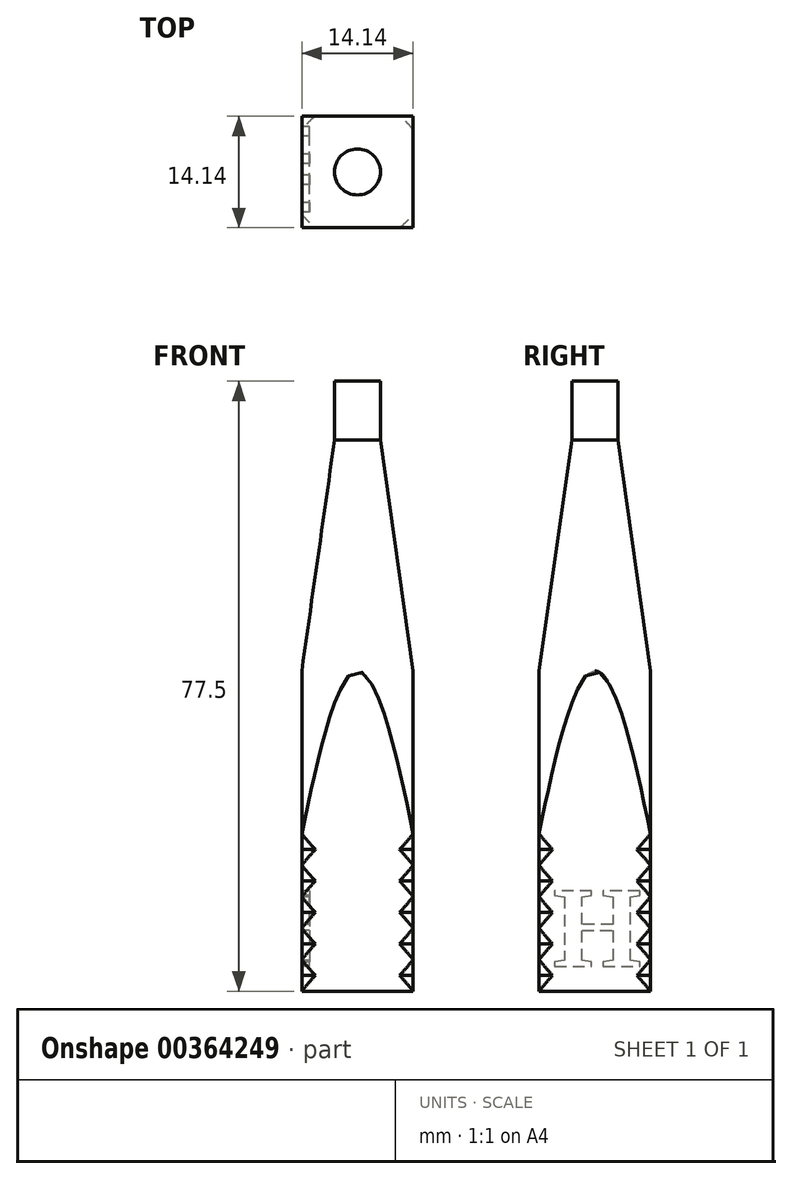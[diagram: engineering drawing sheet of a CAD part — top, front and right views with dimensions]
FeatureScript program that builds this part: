
annotation { "Feature Type Name" : "Feature", "Feature Type Description" : "" }
export const myFeature = defineFeature(function(context is Context, id is Id, definition is map)
    precondition{}
    {
        {
            var Q0;
            Q0=qCreatedBy(makeId("Top.planeOp"),FACE);
            var sketch = newSketch(context, id + "F0", { "sketchPlane" : qUnion([Q0])});
            skCircle(sketch, "E0", {"center": v(0, 0) * mm, "radius": 10 * mm, "construction": true});
            skLineSegment(sketch, "E1", {"start": v(-7.07, -7.07) * mm, "end": v(7.07, -7.07) * mm});
            skLineSegment(sketch, "E2", {"start": v(7.07, -7.07) * mm, "end": v(7.07, 7.07) * mm});
            skLineSegment(sketch, "E3", {"start": v(7.07, 7.07) * mm, "end": v(-7.07, 7.07) * mm});
            skLineSegment(sketch, "E4", {"start": v(-7.07, 7.07) * mm, "end": v(-7.07, -7.07) * mm});
            skSolve(sketch);
        }
        {
            var Q0;
            Q0=makeQuery(id+"F0.imprint","IMPRINT",FACE,{"disambiguationData":[TD([[makeQuery(id+"F0.imprint","IMPRINT",EDGE,{"derivedFrom":sQuery(id+"F0.wireOp",EDGE,"wcAVtdV2-EokJ-VWxA-gxln-DFa8Tj28oSSP")}),-1.0]])]});
            var Q1;
            Q1=makeQuery(id+"F0.imprint","IMPRINT",FACE,{"disambiguationData":[TD([[makeQuery(id+"F0.imprint","IMPRINT",EDGE,{"derivedFrom":sQuery(id+"F0.wireOp",EDGE,"E1")}),1.0]])]});
            extrude(context, id + "F1", {"entities" : qUnion([Q0, Q1]), "offsetDistance" : 25 * mm, "depth" : 20 * mm});
        }
        {
            var Q0;
            Q0=qCreatedBy(makeId("Right.planeOp"),FACE);
            var sketch = newSketch(context, id + "F2", { "sketchPlane" : qUnion([Q0]), "disableImprinting" : false});
            skLineSegment(sketch, "E5", {"start": v(-2.92, 70) * mm, "end": v(-10, 20) * mm});
            skLineSegment(sketch, "E6", {"start": v(-10, 20) * mm, "end": v(0, 20) * mm});
            skLineSegment(sketch, "E7", {"start": v(0, 20) * mm, "end": v(0, 70) * mm});
            skLineSegment(sketch, "E8", {"start": v(-2.92, 70) * mm, "end": v(0, 70) * mm, "construction": true});
            skLineSegment(sketch, "E9", {"start": v(-2.92, 70) * mm, "end": v(-2.92, 76.5) * mm});
            skLineSegment(sketch, "E10", {"start": v(-2.92, 76.5) * mm, "end": v(0, 76.5) * mm});
            skLineSegment(sketch, "E11", {"start": v(0, 76.5) * mm, "end": v(0, 70) * mm});
            skSolve(sketch);
        }
        {
            var Q0;
            Q0=makeQuery(id+"F2.imprint","IMPRINT",FACE,{"disambiguationData":[TD([[makeQuery(id+"F2.imprint","IMPRINT",EDGE,{"derivedFrom":sQuery(id+"F2.wireOp",EDGE,"E5")}),1.0]])]});
            var Q1;
            Q1=sQuery(id+"F2.wireOp",EDGE,"E7");
            revolve(context, id + "F3", {"operationType" : NewBodyOperationType.ADD, "surfaceOperationType" : NewSurfaceOperationType.NEW, "entities" : qUnion([Q0]), "axis" : qUnion([Q1]), "revolveType" : RevolveType.FULL});
        }
        {
            var Q0;
            {var subQ0=makeQuery(id+"F3.opRevolve","SWEPT_FACE",FACE,{"disambiguationData":[OSD([sQuery(id+"F2.wireOp",EDGE,"E6")])]});Q0=makeQuery(id+"F3.boolean.opBoolean","SPLIT",FACE,{"disambiguationData":[TD([makeQuery(id+"F1.opExtrude","SWEPT_FACE",FACE,{"disambiguationData":[OSD([sQuery(id+"F0.wireOp",EDGE,"DRX1ucCg-DjaC-MiWL-Vcy4-4rUpKsN5Zpb4")])]}),makeQuery(id+"F1.opExtrude","SWEPT_FACE",FACE,{"disambiguationData":[OSD([sQuery(id+"F0.wireOp",EDGE,"OoSLFpEq-8l7p-tjY5-sLpR-2C7ZDxoHFw3J")])]}),makeQuery(id+"F1.opExtrude","SWEPT_FACE",FACE,{"disambiguationData":[OSD([sQuery(id+"F0.wireOp",EDGE,"05nhAoml-3LFM-mqCG-1RSL-4N1tzizKSWDP")])]}),makeQuery(id+"F3.opRevolve","SWEPT_FACE",FACE,{"disambiguationData":[OSD([sQuery(id+"F2.wireOp",EDGE,"E5")])]}),subQ0])],"derivedFrom":subQ0});}
            var Q1;
            {var subQ0=makeQuery(id+"F3.opRevolve","SWEPT_FACE",FACE,{"disambiguationData":[OSD([sQuery(id+"F2.wireOp",EDGE,"E6")])]});Q1=makeQuery(id+"F3.boolean.opBoolean","SPLIT",FACE,{"disambiguationData":[TD([makeQuery(id+"F1.opExtrude","SWEPT_FACE",FACE,{"disambiguationData":[OSD([sQuery(id+"F0.wireOp",EDGE,"wcAVtdV2-EokJ-VWxA-gxln-DFa8Tj28oSSP")])]}),makeQuery(id+"F1.opExtrude","SWEPT_FACE",FACE,{"disambiguationData":[OSD([sQuery(id+"F0.wireOp",EDGE,"OoSLFpEq-8l7p-tjY5-sLpR-2C7ZDxoHFw3J")])]}),makeQuery(id+"F1.opExtrude","SWEPT_FACE",FACE,{"disambiguationData":[OSD([sQuery(id+"F0.wireOp",EDGE,"05nhAoml-3LFM-mqCG-1RSL-4N1tzizKSWDP")])]}),makeQuery(id+"F3.opRevolve","SWEPT_FACE",FACE,{"disambiguationData":[OSD([sQuery(id+"F2.wireOp",EDGE,"E5")])]}),subQ0])],"derivedFrom":subQ0});}
            var Q2;
            {var subQ0=makeQuery(id+"F3.opRevolve","SWEPT_FACE",FACE,{"disambiguationData":[OSD([sQuery(id+"F2.wireOp",EDGE,"E6")])]});Q2=makeQuery(id+"F3.boolean.opBoolean","SPLIT",FACE,{"disambiguationData":[TD([makeQuery(id+"F1.opExtrude","SWEPT_FACE",FACE,{"disambiguationData":[OSD([sQuery(id+"F0.wireOp",EDGE,"tCxQUq4m-YUaR-PUol-IUOQ-F8SX8qTUi1zU")])]}),makeQuery(id+"F1.opExtrude","SWEPT_FACE",FACE,{"disambiguationData":[OSD([sQuery(id+"F0.wireOp",EDGE,"DRX1ucCg-DjaC-MiWL-Vcy4-4rUpKsN5Zpb4")])]}),makeQuery(id+"F1.opExtrude","SWEPT_FACE",FACE,{"disambiguationData":[OSD([sQuery(id+"F0.wireOp",EDGE,"OoSLFpEq-8l7p-tjY5-sLpR-2C7ZDxoHFw3J")])]}),makeQuery(id+"F3.opRevolve","SWEPT_FACE",FACE,{"disambiguationData":[OSD([sQuery(id+"F2.wireOp",EDGE,"E5")])]}),subQ0])],"derivedFrom":subQ0});}
            var Q3;
            {var subQ0=makeQuery(id+"F3.opRevolve","SWEPT_FACE",FACE,{"disambiguationData":[OSD([sQuery(id+"F2.wireOp",EDGE,"E6")])]});Q3=makeQuery(id+"F3.boolean.opBoolean","SPLIT",FACE,{"disambiguationData":[TD([makeQuery(id+"F1.opExtrude","SWEPT_FACE",FACE,{"disambiguationData":[OSD([sQuery(id+"F0.wireOp",EDGE,"Q6e6Ubm2-IwZc-4Gsr-nhjH-oOF9pMSWuxT1")])]}),makeQuery(id+"F1.opExtrude","SWEPT_FACE",FACE,{"disambiguationData":[OSD([sQuery(id+"F0.wireOp",EDGE,"tCxQUq4m-YUaR-PUol-IUOQ-F8SX8qTUi1zU")])]}),makeQuery(id+"F1.opExtrude","SWEPT_FACE",FACE,{"disambiguationData":[OSD([sQuery(id+"F0.wireOp",EDGE,"DRX1ucCg-DjaC-MiWL-Vcy4-4rUpKsN5Zpb4")])]}),makeQuery(id+"F3.opRevolve","SWEPT_FACE",FACE,{"disambiguationData":[OSD([sQuery(id+"F2.wireOp",EDGE,"E5")])]}),subQ0])],"derivedFrom":subQ0});}
            var Q4;
            {var subQ0=makeQuery(id+"F3.opRevolve","SWEPT_FACE",FACE,{"disambiguationData":[OSD([sQuery(id+"F2.wireOp",EDGE,"E6")])]});Q4=makeQuery(id+"F3.boolean.opBoolean","SPLIT",FACE,{"disambiguationData":[TD([makeQuery(id+"F1.opExtrude","SWEPT_FACE",FACE,{"disambiguationData":[OSD([sQuery(id+"F0.wireOp",EDGE,"wcAVtdV2-EokJ-VWxA-gxln-DFa8Tj28oSSP")])]}),makeQuery(id+"F1.opExtrude","SWEPT_FACE",FACE,{"disambiguationData":[OSD([sQuery(id+"F0.wireOp",EDGE,"Q6e6Ubm2-IwZc-4Gsr-nhjH-oOF9pMSWuxT1")])]}),makeQuery(id+"F1.opExtrude","SWEPT_FACE",FACE,{"disambiguationData":[OSD([sQuery(id+"F0.wireOp",EDGE,"tCxQUq4m-YUaR-PUol-IUOQ-F8SX8qTUi1zU")])]}),makeQuery(id+"F3.opRevolve","SWEPT_FACE",FACE,{"disambiguationData":[OSD([sQuery(id+"F2.wireOp",EDGE,"E5")])]}),subQ0])],"derivedFrom":subQ0});}
            var Q5;
            {var subQ0=makeQuery(id+"F3.opRevolve","SWEPT_FACE",FACE,{"disambiguationData":[OSD([sQuery(id+"F2.wireOp",EDGE,"E6")])]});Q5=makeQuery(id+"F3.boolean.opBoolean","SPLIT",FACE,{"disambiguationData":[TD([makeQuery(id+"F1.opExtrude","SWEPT_FACE",FACE,{"disambiguationData":[OSD([sQuery(id+"F0.wireOp",EDGE,"wcAVtdV2-EokJ-VWxA-gxln-DFa8Tj28oSSP")])]}),makeQuery(id+"F1.opExtrude","SWEPT_FACE",FACE,{"disambiguationData":[OSD([sQuery(id+"F0.wireOp",EDGE,"Q6e6Ubm2-IwZc-4Gsr-nhjH-oOF9pMSWuxT1")])]}),makeQuery(id+"F1.opExtrude","SWEPT_FACE",FACE,{"disambiguationData":[OSD([sQuery(id+"F0.wireOp",EDGE,"05nhAoml-3LFM-mqCG-1RSL-4N1tzizKSWDP")])]}),makeQuery(id+"F3.opRevolve","SWEPT_FACE",FACE,{"disambiguationData":[OSD([sQuery(id+"F2.wireOp",EDGE,"E5")])]}),subQ0])],"derivedFrom":subQ0});}
            extrude(context, id + "F4", {"entities" : qUnion([Q0, Q1, Q2, Q3, Q4, Q5]), "operationType" : NewBodyOperationType.REMOVE, "oppositeDirection" : true, "offsetDistance" : 25 * mm, "depth" : 25 * mm});
        }
        {
            var Q0;
            Q0=qCreatedBy(makeId("Front.planeOp"),FACE);
            var sketch = newSketch(context, id + "F5", { "sketchPlane" : qUnion([Q0])});
            skLineSegment(sketch, "E12", {"start": v(-10, 20) * mm, "end": v(-10, 0) * mm});
            skLineSegment(sketch, "E13", {"start": v(-10, 20) * mm, "end": v(-8.86, 18) * mm});
            skLineSegment(sketch, "E14", {"start": v(-8.86, 18) * mm, "end": v(-10, 16) * mm});
            skLineSegment(sketch, "E15", {"start": v(-10, 20) * mm, "end": v(-10, 16) * mm, "construction": true});
            skLineSegment(sketch, "E16.0.1.0", {"start": v(-10, 16) * mm, "end": v(-8.86, 14) * mm});
            skLineSegment(sketch, "E16.0.1.1", {"start": v(-8.86, 14) * mm, "end": v(-10, 12) * mm});
            skLineSegment(sketch, "E16.0.2.0", {"start": v(-10, 12) * mm, "end": v(-8.86, 10) * mm});
            skLineSegment(sketch, "E16.0.2.1", {"start": v(-8.86, 10) * mm, "end": v(-10, 8) * mm});
            skLineSegment(sketch, "E16.0.3.0", {"start": v(-10, 8) * mm, "end": v(-8.86, 6) * mm});
            skLineSegment(sketch, "E16.0.3.1", {"start": v(-8.86, 6) * mm, "end": v(-10, 4) * mm});
            skLineSegment(sketch, "E16.0.4.0", {"start": v(-10, 4) * mm, "end": v(-8.86, 2) * mm});
            skLineSegment(sketch, "E16.0.4.1", {"start": v(-8.86, 2) * mm, "end": v(-10, 0) * mm});
            skLineSegment(sketch, "E16.direction1", {"start": v(-10, 20) * mm, "end": v(15, 20) * mm, "construction": true});
            skLineSegment(sketch, "E17", {"start": v(0, 11.1) * mm, "end": v(0, 0) * mm, "construction": true});
            skLineSegment(sketch, "E18", {"start": v(-8.86, 18) * mm, "end": v(-10, 18) * mm, "construction": true});
            skLineSegment(sketch, "E19", {"start": v(-8.86, 14) * mm, "end": v(-10, 14) * mm, "construction": true});
            skLineSegment(sketch, "E20", {"start": v(-8.86, 10) * mm, "end": v(-10, 10) * mm, "construction": true});
            skLineSegment(sketch, "E21", {"start": v(-8.86, 6) * mm, "end": v(-10, 6) * mm, "construction": true});
            skLineSegment(sketch, "E22", {"start": v(-8.86, 2) * mm, "end": v(-10, 2) * mm, "construction": true});
            skSolve(sketch);
        }
        {
            var Q0;
            Q0=qSketchRegion(id+"F5",true);
            var Q1;
            Q1=sQuery(id+"F5.wireOp",EDGE,"E17");
            revolve(context, id + "F6", {"operationType" : NewBodyOperationType.REMOVE, "entities" : qUnion([Q0]), "axis" : qUnion([Q1]), "revolveType" : RevolveType.FULL});
        }
        {
            var Q0;
            Q0=makeQuery(id+"F3.opRevolve","SWEPT_FACE",FACE,{"disambiguationData":[OSD([sQuery(id+"F2.wireOp",EDGE,"E10")])]});
            extrude(context, id + "F7", {"entities" : qUnion([Q0]), "operationType" : NewBodyOperationType.ADD, "offsetDistance" : 25 * mm, "depth" : 1 * mm});
        }
        {
            var Q0;
            {var subQ0=sQuery(id+"F0.wireOp",EDGE,"E4");Q0=makeQuery(id+"F4.boolean.opBoolean","MERGE",FACE,{"derivedFrom":[makeQuery(id+"F1.opExtrude","SWEPT_FACE",FACE,{"disambiguationData":[OSD([subQ0])]})],"fromTools":[makeQuery(id+"F4.opExtrude","SWEPT_FACE",FACE,{"disambiguationData":[OSD([subQ0])]})]});}
            var sketch = newSketch(context, id + "F8", { "sketchPlane" : qUnion([Q0])});
            skText(sketch, "E23", { "text": "H", "fontName": "Tinos-Bold.ttf"});
            const initialGuessF8  = {"E23": [-0.006, 0.00318, 1, 0, 0.01049]};
            skSetInitialGuess(sketch, initialGuessF8);
            skSolve(sketch);
        }
        {
            var Q0;
            Q0=makeQuery(id+"F8.imprint","IMPRINT",FACE,{"disambiguationData":[TD([[makeQuery(id+"F8.imprint","IMPRINT",EDGE,{"derivedFrom":sQuery(id+"F8.wireOp",EDGE,"E23.sketch_text.stroke-0")}),-1.0]])]});
            extrude(context, id + "F9", {"entities" : qUnion([Q0]), "operationType" : NewBodyOperationType.REMOVE, "oppositeDirection" : true, "depth" : 1 * mm, "offsetDistance" : 25 * mm});
        }
        {
            var Q0;
            Q0=qCreatedBy(makeId("Right.planeOp"),FACE);
            var sketch = newSketch(context, id + "F10", { "sketchPlane" : qUnion([Q0])});
            skLineSegment(sketch, "E24", {"start": v(0, 0) * mm, "end": v(0, -17.2) * mm, "construction": true});
            skSolve(sketch);
        }
    });
